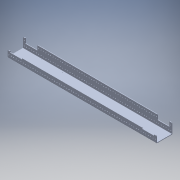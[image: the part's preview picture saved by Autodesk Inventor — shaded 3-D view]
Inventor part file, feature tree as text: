
AUTODESK INVENTOR PART (.ipt)
format: ipt  version: 2017 (Build 210142000, 142)  size: 342,528 bytes
history: native  units: in
note: dims shown in document units (in); Inventor stores cm internally (conversion verified against a paired STEP export)
features: other x5, reference x2, extrude x1, sketch x1
ambient origin geometry x8: Origin, YZ Plane, XZ Plane, XY Plane, X Axis, Y Axis, Z Axis, Center Point
bodies: Solid1 (feature_tree)
feature tree (9):
  extrude  "Extrusion1"  Depth=0.5in
  sketch  "Sketch1"  dims[d0=1.0in d1=0.0in d2=0.5in d3=0.5in d4=1.0in]
  reference  "Reference1"
  reference  "Reference2"
  other  "LPattern4"
  other  "<userpath>\Documents\Inventor\2017 Robot\Robot Chassis.iam"
  other  "Robot Chassis.iam"
  other  "am-2951a_AM14U3_Outside_Plate:1"
  other  "am-2952a_AM14U3_Inside_Plate:1"
